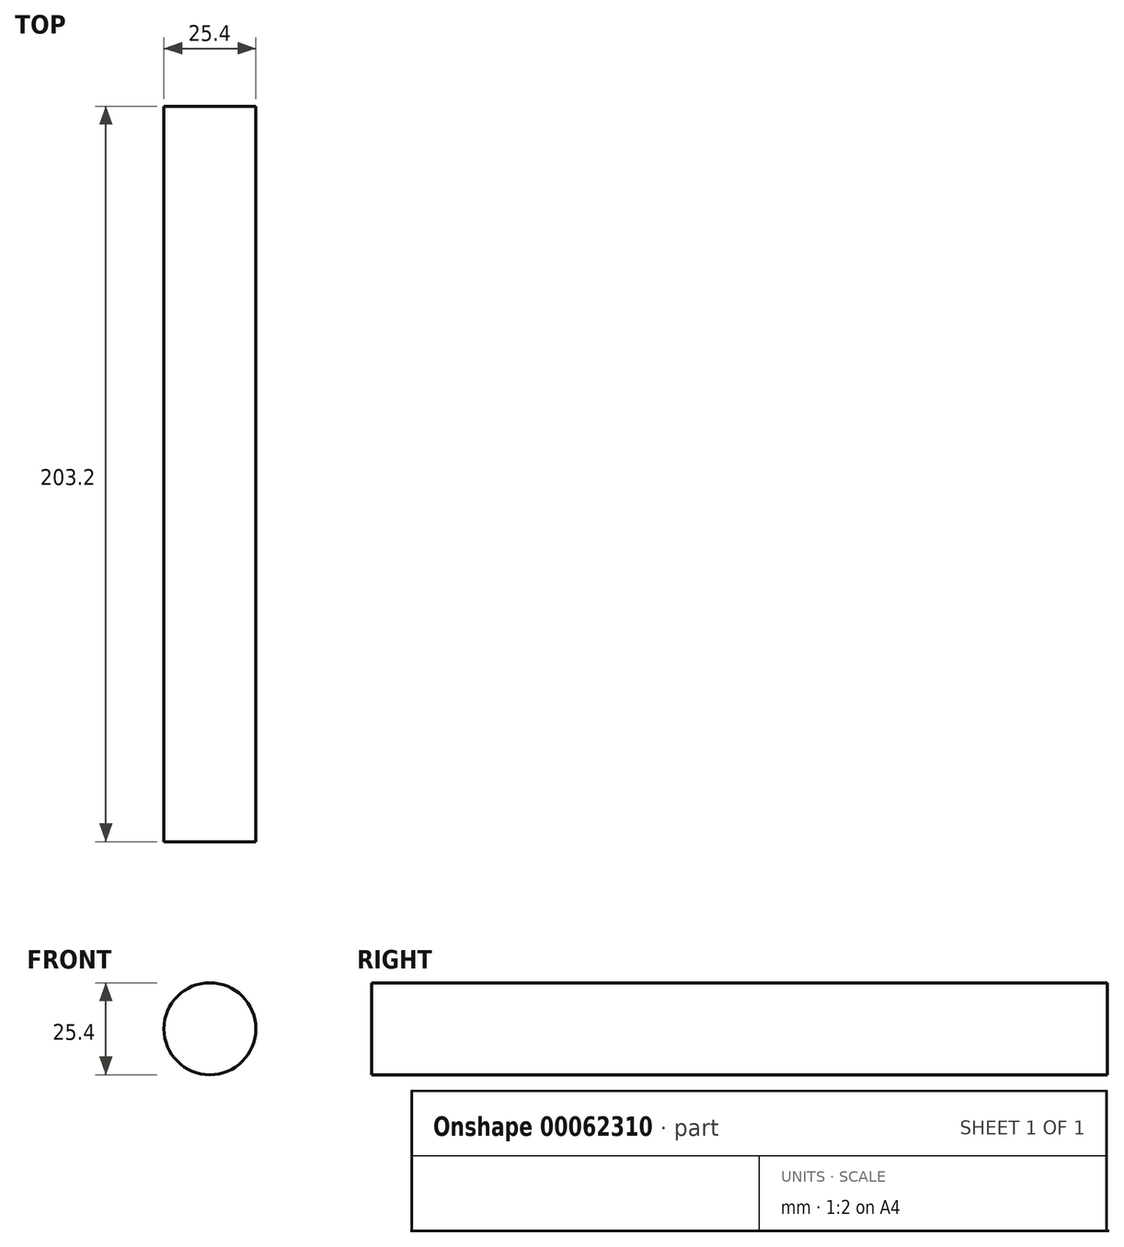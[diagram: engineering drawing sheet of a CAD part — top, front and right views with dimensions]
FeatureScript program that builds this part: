
annotation { "Feature Type Name" : "Feature", "Feature Type Description" : "" }
export const myFeature = defineFeature(function(context is Context, id is Id, definition is map)
    precondition{}
    {
        {
            var Q0;
            Q0=qCreatedBy(makeId("Front.planeOp"),FACE);
            var sketch = newSketch(context, id + "F0", { "sketchPlane" : qUnion([Q0])});
            skCircle(sketch, "E0", {"center": v(0, 0) * mm, "radius": 12.7 * mm});
            skSolve(sketch);
        }
        {
            var Q0;
            Q0 = qSketchRegion(id + "F0", true);
            extrude(context, id + "F1", {"entities" : qUnion([Q0]), "endBound" : BoundingType.SYMMETRIC, "depth" : 203.2 * mm});
        }
    });
